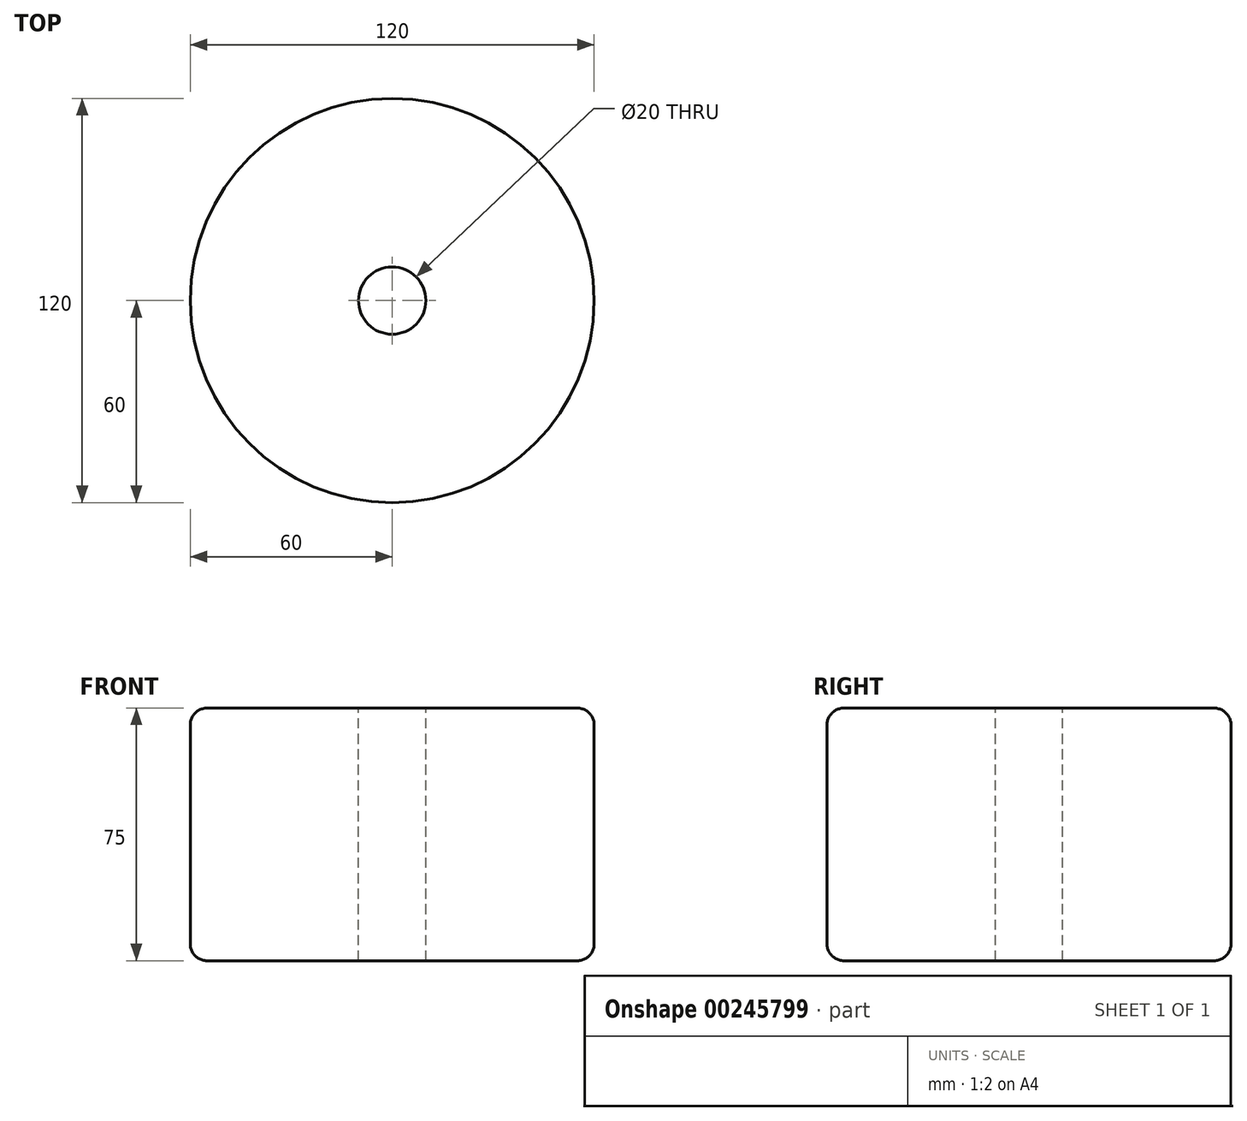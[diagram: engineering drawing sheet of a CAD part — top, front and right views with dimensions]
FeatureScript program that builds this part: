
annotation { "Feature Type Name" : "Feature", "Feature Type Description" : "" }
export const myFeature = defineFeature(function(context is Context, id is Id, definition is map)
    precondition{}
    {
        {
            var Q0;
            Q0=qCreatedBy(makeId("Front.planeOp"),FACE);
            var sketch = newSketch(context, id + "F0", { "sketchPlane" : qUnion([Q0])});
            skLineSegment(sketch, "E0", {"start": v(0, 72.35) * mm, "end": v(0, -59.17) * mm, "construction": true});
            skLineSegment(sketch, "E1", {"start": v(-87.26, 0) * mm, "end": v(83.67, 0) * mm, "construction": true});
            skLineSegment(sketch, "E2.bottom", {"start": v(10, 37.5) * mm, "end": v(60, 37.5) * mm});
            skLineSegment(sketch, "E2.top", {"start": v(10, -37.5) * mm, "end": v(60, -37.5) * mm});
            skLineSegment(sketch, "E2.right", {"start": v(60, 37.5) * mm, "end": v(60, -37.5) * mm});
            skLineSegment(sketch, "E3", {"start": v(10, 37.5) * mm, "end": v(10, -37.5) * mm});
            skPoint(sketch, "E4", {"position": v(60, 0) * mm});
            skSolve(sketch);
        }
        {
            var Q0;
            Q0 = qSketchRegion(id + "F0", true);
            var Q1;
            Q1=sQuery(id+"F0.wireOp",EDGE,"E0");
            revolve(context, id + "F1", {"entities" : qUnion([Q0]), "axis" : qUnion([Q1]), "revolveType" : RevolveType.FULL});
        }
        {
            var Q0;
            Q0=makeQuery(id+"F1.opRevolve","SWEPT_EDGE",EDGE,{"disambiguationData":[OSD([sQuery(id+"F0.wireOp",EDGE,"E2.bottom"),sQuery(id+"F0.wireOp",EDGE,"E2.right")])]});
            var Q1;
            Q1=makeQuery(id+"F1.opRevolve","SWEPT_EDGE",EDGE,{"disambiguationData":[OSD([sQuery(id+"F0.wireOp",EDGE,"E2.top"),sQuery(id+"F0.wireOp",EDGE,"E2.right")])]});
            fillet(context, id + "F2", {"entities" : qUnion([Q0, Q1]), "radius" : 5 * mm, "tangentPropagation" : true, "allowEdgeOverflow" : false});
        }
    });
